# Revit family: AFX-Pearl_Sconce-
name_source: partatom
category: Lighting Fixtures
units: mm (PartAtom-declared; Revit-internal decimal feet)

## family parameters
Cut with Voids When Loaded = No
Host = Face
Light Source = Yes
Part Type = Normal
Room Calculation Point = No
Round Connector Dimension = Use Diameter
Shared = No

## types (2) — shared parameters
Apparent Load = 0 VA
Assembly Code = D5020200
Color Filter = 16777215
Colour Rendering Index = 90
Cover Finish = AFX - Black Steel
Default Elevation = 48"
Depth = 4"
Diffuser Finish = AFX - White Acrylic
Dimming Lamp Color Temperature Shift = <None>
Dist Support = 1 37/64"
Frame Finish = AFX - Black Steel
Grommet Cap Finish = AFX - Black Steel
Housing Finish = AFX - Black Steel
Keynote = 12500
LED Finish = AFX - White Plastic
Manufacturer = AFX Inc
Product Documentation Link = https://www.afxinc.com
Revit File Built By = https://servex-us.com
Tilt Angle = 0.00°
Type Comments = Pearl
URL = https://www.afxinc.com
Voltage = 120 V
Width = 4 3/8"

## per-type parameters (varying)
| type | Description | Dist Light Source | Height | Lower Dist | P01 | P02 | Photometric Web File | Upper Dist | Wattage Comments |
| PRLS0409L30D1BK | Simplistic LED sconce with white glass globe with 1 Light and vertical or horizontal mounting - 4 3/8"W x 4"D x 8 1/2"H | 3 37/64" | 8 1/2" | 2 31/64" | Yes | No | PRLS0409L30D1XX.IES | 1 49/64" | 7.5 |
| PRLS0418L30D1BK | Simplistic LED sconce with white glass globe with 2 Lights and vertical or horizontal mounting - 4 3/8"W x 4"D x 17 1/4"H | 9 1/2" | 17 1/4" | 4 27/32" | No | Yes | PRLS0418L30D1XX.IES | 4 27/32" | 13 |

note: column(s) folded — value = type name in every type: Model

## geometry (parser evidence)
native form markers: Sweep x1
no freeform markers — native parametric forms only
